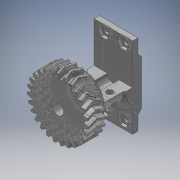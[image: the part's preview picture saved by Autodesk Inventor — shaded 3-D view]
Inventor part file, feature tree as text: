
AUTODESK INVENTOR PART (.ipt)
format: ipt  version: 2019 (Build 230136000, 136)  size: 915,968 bytes
history: native  units: mm (DEFAULTED — no unit token found)
features: sketch x18, extrude x12, plane x8, hole x5, chamfer x4, other x3, mirror x3
ambient origin geometry x8: Origin, YZ Plane, XZ Plane, XY Plane, X Axis, Y Axis, Z Axis, Center Point
bodies: Solid1 (feature_tree)
feature tree (53):
  extrude  "Extrusion1"  Depth=5.0mm TaperAngle=0.0deg
  plane  "Work Plane2"
  plane  "Work Plane8"
  plane  "Work Plane9"
  other  "Spur Gear"
  mirror  "Mirror1"
  plane  "Work Plane11"
  extrude  "Extrusion2"  Depth=10.0mm TaperAngle=0.0deg
  extrude  "Extrusion3"  Depth=1.163553mm TaperAngle=0.0deg
  chamfer  "Chamfer1"  [1 undecoded]
  hole  "Hole1"  [1 undecoded]
  hole  "Hole2"  [1 undecoded]
  extrude  "Extrusion4"  Depth=3.75mm TaperAngle=45.0deg
  plane  "Work Plane13"
  extrude  "Extrusion5"  Depth=10.0mm
  plane  "Work Plane14"
  hole  "Hole3"  [1 undecoded]
  plane  "Work Plane15"
  hole  "Hole4"  [1 undecoded]
  extrude  "Extrusion6"  Depth=10.0mm
  extrude  "Extrusion7"  [1 undecoded]
  chamfer  "Chamfer2"  Distance=5.5mm
  extrude  "Extrusion9"  Depth=10.0mm TaperAngle=0.0deg
  extrude  "Extrusion10"  Depth=10.0mm TaperAngle=0.0deg
  chamfer  "Chamfer4"  Distance=0.75mm Angle=45.0deg
  extrude  "Extrusion11"  Depth=10.0mm
  hole  "Hole5"  [1 undecoded]
  extrude  "Extrusion12"  Depth=10.0mm TaperAngle=0.0deg
  mirror  "Mirror2"
  plane  "Work Plane16"
  extrude  "Extrusion13"  Depth=10.0mm
  mirror  "Mirror3"
  chamfer  "Chamfer6"  Distance=10.0mm
  sketch  "Sketch1"  dims[d0=34.130032mm d1=5.0mm d2=0.0mm]
  sketch  "Sketch2"  dims[d3=31.880377mm d4=10.0mm d5=0.0mm]
  other  "Srf1"
  sketch  "Sketch6"  dims[d16=31.29mm d17=0.0mm d34=1.163553mm]
  sketch  "Sketch7"  dims[d39=0.0mm]
  sketch  "Sketch9"  dims[d41=0.0mm]
  sketch  "Sketch10"  dims[d43=31.29mm]
  sketch  "Sketch11"  dims[d46=31.29mm d47=0.0mm d48=0.0mm]
  sketch  "Sketch12"  dims[d49=5.0mm d52=29.0mm]
  sketch  "Sketch13"  dims[d53=20.0mm d54=0.0mm d55=20.0mm]
  sketch  "Sketch14"  dims[d56=15.0mm d57=0.0mm d58=3.75mm d59=2.0mm d60=45.0deg]
  sketch  "Sketch15"  dims[d61=7.5mm d62=6.0mm d63=4.0mm d64=2.0mm d65=90.0deg d66=8.0mm d67=20.594885mm]
  sketch  "Sketch16"  dims[d68=6.5mm d69=6.0mm d70=4.0mm d71=2.0mm d72=90.0deg d73=8.0mm d74=0.0mm d75=10.0mm]
  sketch  "Sketch18"  dims[d76=1.0mm d77=10.0mm d78=0.0mm]
  sketch  "Sketch19"  dims[d79=10.0mm d80=1.0mm]
  sketch  "Sketch20"  dims[d81=20.0mm d82=0.0mm d83=10.0mm]
  sketch  "Sketch21"  dims[d84=3.5mm]
  sketch  "Sketch22"  dims[d85=3.5mm d86=6.0mm d87=6.0mm d88=7.0mm d89=90.0deg d90=8.0mm d91=0.0mm d92=-10.0mm]
  sketch  "Sketch23"  dims[d93=3.5mm d94=6.0mm d95=4.0mm d96=5.0mm d97=90.0deg d98=8.0mm d99=0.0mm d100=5.5mm d101=8.0mm d102=0.0mm d103=1.0mm d104=0.0mm d110=0.75mm d111=2.0mm d112=45.0deg d116=21.5mm d117=45.1mm d118=5.0mm d119=0.0mm d120=10.0mm d121=10.0mm d122=2.0mm d123=0.0mm d124=2.0mm d125=2.0mm d126=45.0deg d127=2.0mm d128=0.0mm d132=3.5mm d133=6.0mm d134=4.0mm d135=5.0mm d136=90.0deg d137=8.0mm d138=0.0mm d139=5.5mm d140=5.5mm d141=1.75mm d142=0.0mm d143=10.0mm d144=1.75mm d145=0.0mm d146=4.5mm d147=2.0mm d148=45.0deg]
  other  "Pitch Diameter"
note: 7 required parameter values undecoded (feature->parameter linkage not recoverable at this tier; creation-order binding heuristic only, values carry confidence <= 0.55)
